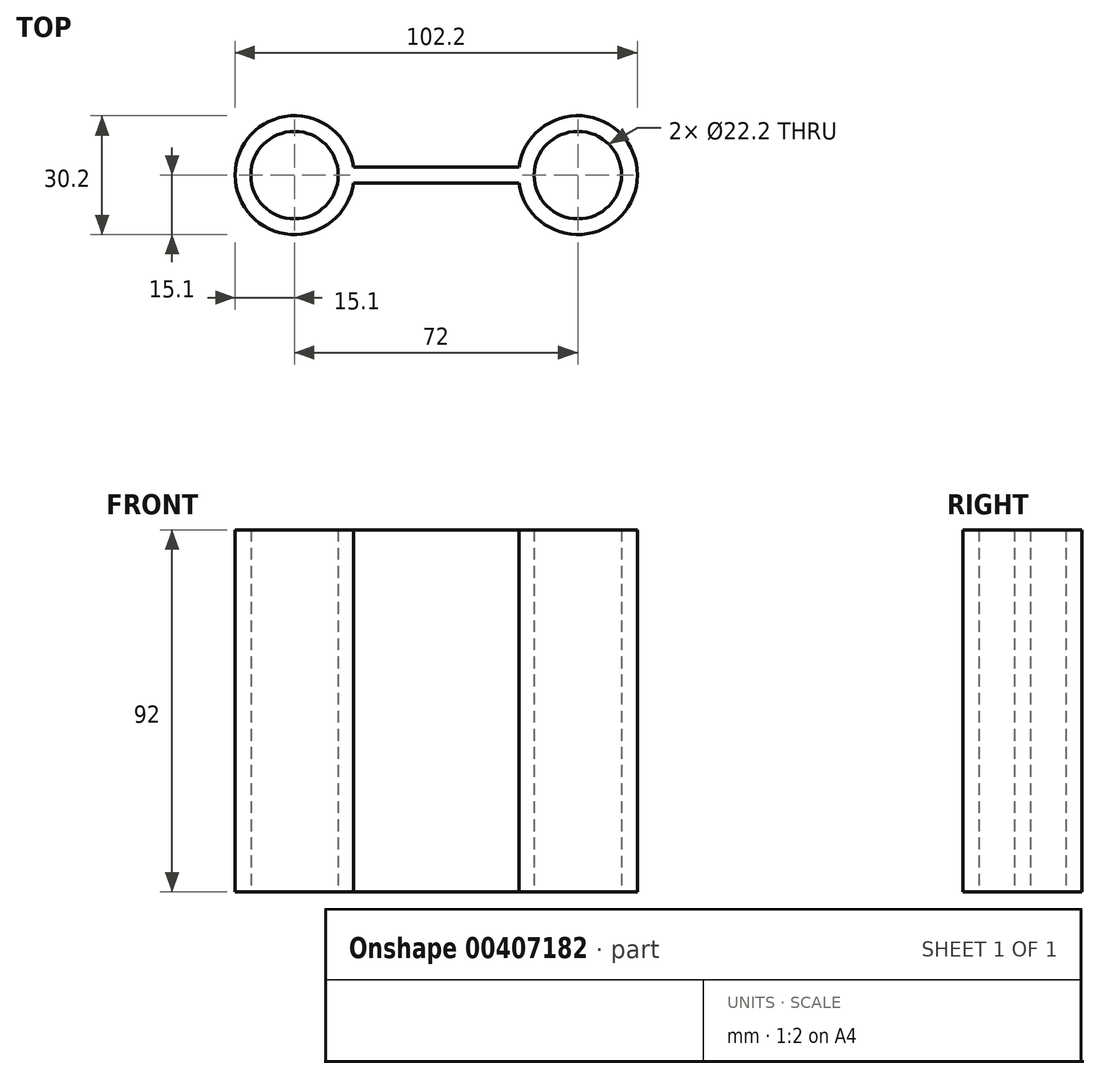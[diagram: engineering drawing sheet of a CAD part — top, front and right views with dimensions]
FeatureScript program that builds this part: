
annotation { "Feature Type Name" : "Feature", "Feature Type Description" : "" }
export const myFeature = defineFeature(function(context is Context, id is Id, definition is map)
    precondition{}
    {
        {
            var Q0;
            Q0=qCreatedBy(makeId("Top.planeOp"),FACE);
            var sketch = newSketch(context, id + "F0", { "sketchPlane" : qUnion([Q0])});
            skLineSegment(sketch, "E0.bottom", {"start": v(0, -2) * mm, "end": v(-21.03, -2) * mm});
            skLineSegment(sketch, "E0.top", {"start": v(0, 2) * mm, "end": v(-21.03, 2) * mm});
            skLineSegment(sketch, "E0.left", {"start": v(0, -2) * mm, "end": v(0, 2) * mm, "construction": true});
            skCircle(sketch, "E1", {"center": v(-36, 0) * mm, "radius": 11.1 * mm});
            skArc(sketch, "E2", {"start": v(-21.03, 2) * mm, "mid": v(-51.1, 0) * mm, "end": v(-21.03, -2) * mm});
            skLineSegment(sketch, "E3.MirrorCS", {"start": v(0, -2) * mm, "end": v(21.03, -2) * mm});
            skLineSegment(sketch, "E4.MirrorCS", {"start": v(0, 2) * mm, "end": v(21.03, 2) * mm});
            skCircle(sketch, "E5.MirrorC", {"center": v(36, 0) * mm, "radius": 11.1 * mm});
            skArc(sketch, "E6.MirrorCS", {"start": v(21.03, 2) * mm, "mid": v(51.1, 0) * mm, "end": v(21.03, -2) * mm});
            skSolve(sketch);
        }
        {
            var Q0;
            Q0=makeQuery(id+"F0.imprint","IMPRINT",FACE,{"disambiguationData":[TD([[makeQuery(id+"F0.imprint","IMPRINT",EDGE,{"derivedFrom":sQuery(id+"F0.wireOp",EDGE,"E0.bottom")}),-1.0]])]});
            extrude(context, id + "F1", {"entities" : qUnion([Q0]), "endBound" : BoundingType.SYMMETRIC, "depth" : 92 * mm});
        }
    });
